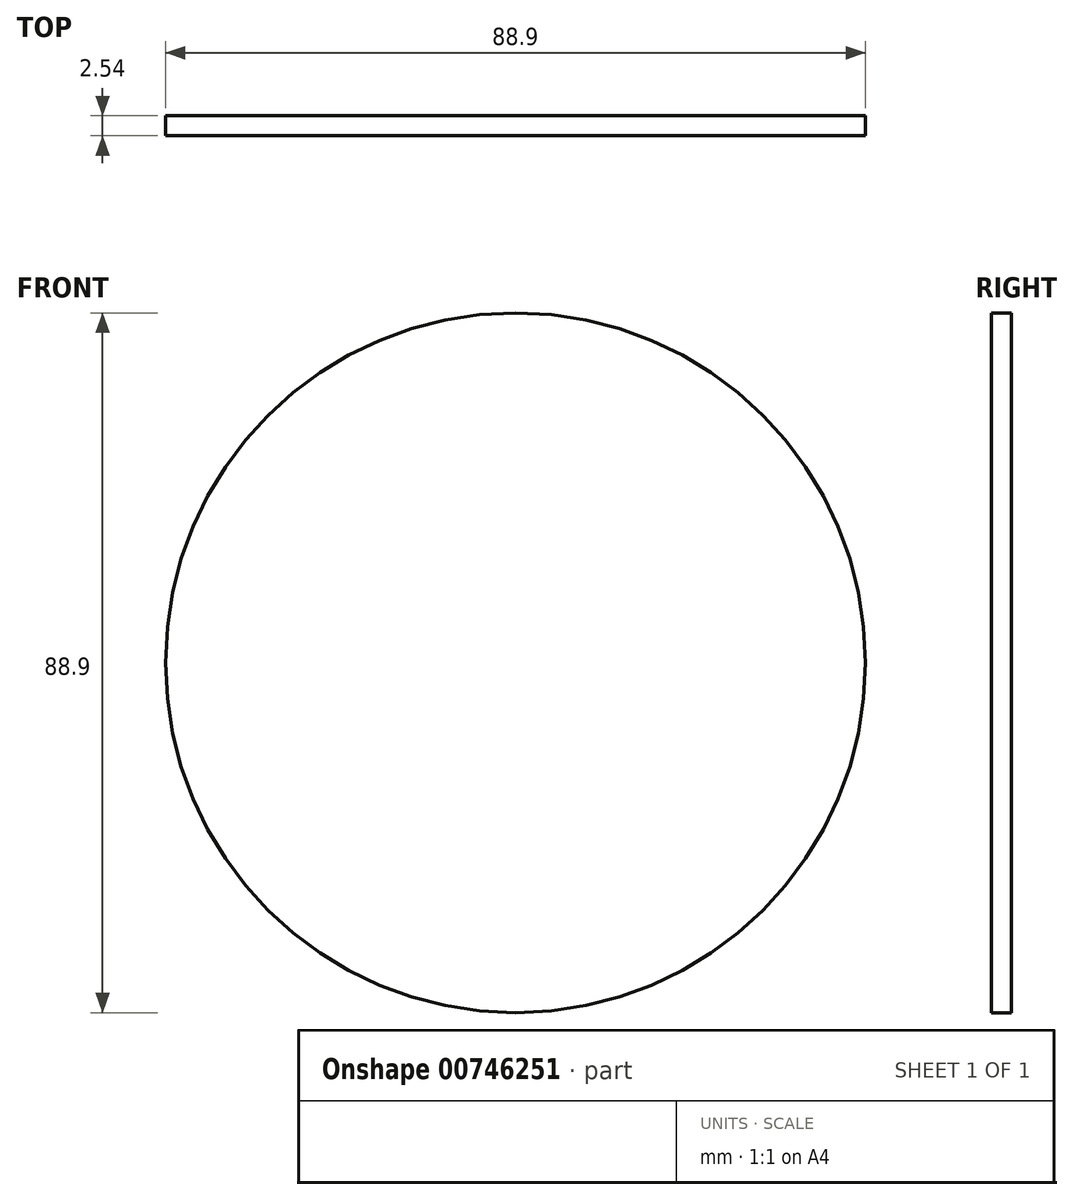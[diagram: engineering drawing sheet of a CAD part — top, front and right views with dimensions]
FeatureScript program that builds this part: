
annotation { "Feature Type Name" : "Feature", "Feature Type Description" : "" }
export const myFeature = defineFeature(function(context is Context, id is Id, definition is map)
    precondition{}
    {
        {
            var Q0;
            Q0=qCreatedBy(makeId("Front.planeOp"),FACE);
            var sketch = newSketch(context, id + "F0", { "sketchPlane" : qUnion([Q0])});
            skCircle(sketch, "E0", {"center": v(0, 0) * mm, "radius": 44.45 * mm});
            skSolve(sketch);
        }
        {
            var Q0;
            Q0=makeQuery(id+"F0.imprint","IMPRINT",FACE,{"disambiguationData":[TD([[makeQuery(id+"F0.imprint","IMPRINT",EDGE,{"derivedFrom":sQuery(id+"F0.wireOp",EDGE,"E0")}),1.0]])]});
            extrude(context, id + "F1", {"entities" : qUnion([Q0]), "depth" : 2.54 * mm, "offsetDistance" : 25.4 * mm});
        }
    });
